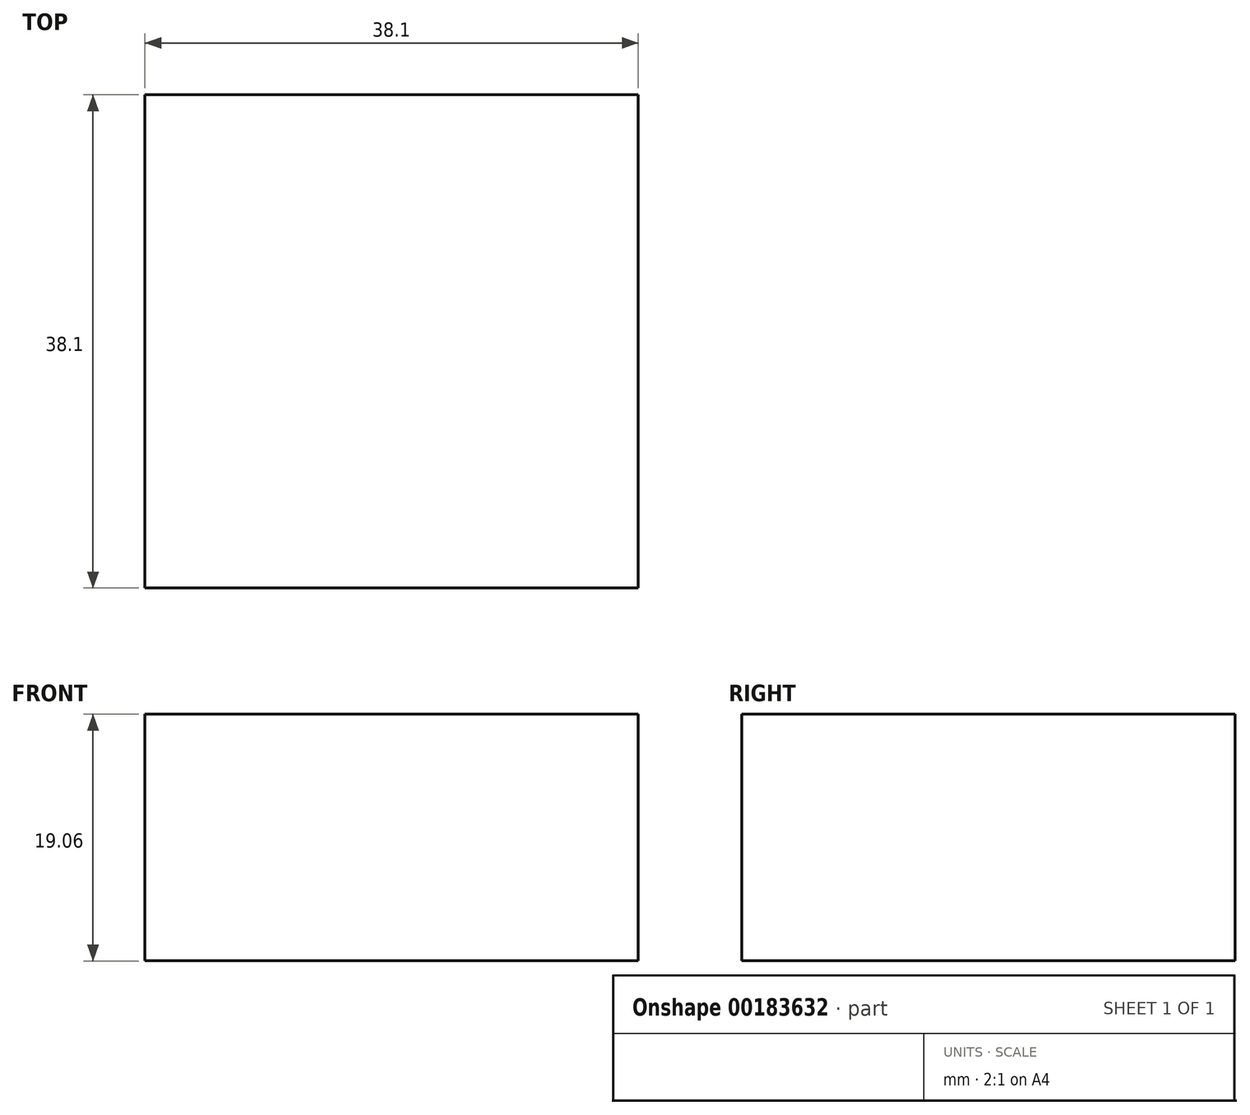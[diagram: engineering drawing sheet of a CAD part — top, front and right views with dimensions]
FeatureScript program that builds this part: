
annotation { "Feature Type Name" : "Feature", "Feature Type Description" : "" }
export const myFeature = defineFeature(function(context is Context, id is Id, definition is map)
    precondition{}
    {
        {
            var Q0;
            Q0=qCreatedBy(makeId("Front.planeOp"),FACE);
            var sketch = newSketch(context, id + "F0", { "sketchPlane" : qUnion([Q0])});
            skLineSegment(sketch, "E0.bottom", {"start": v(-19.05, 9.53) * mm, "end": v(19.05, 9.53) * mm});
            skLineSegment(sketch, "E0.top", {"start": v(-19.05, -9.53) * mm, "end": v(19.05, -9.53) * mm});
            skLineSegment(sketch, "E0.left", {"start": v(-19.05, 9.53) * mm, "end": v(-19.05, -9.53) * mm});
            skLineSegment(sketch, "E0.right", {"start": v(19.05, 9.53) * mm, "end": v(19.05, -9.53) * mm});
            skPoint(sketch, "E0.middle", {"position": v(0, 0) * mm});
            skSolve(sketch);
        }
        {
            var Q0;
            Q0=makeQuery(id+"F0.imprint","IMPRINT",FACE,{"disambiguationData":[TD([[makeQuery(id+"F0.imprint","IMPRINT",EDGE,{"derivedFrom":sQuery(id+"F0.wireOp",EDGE,"E0.bottom")}),-1.0]])]});
            extrude(context, id + "F1", {"entities" : qUnion([Q0]), "depth" : 19.05 * mm, "hasSecondDirection" : true, "secondDirectionOppositeDirection" : true, "secondDirectionDepth" : 19.05 * mm});
        }
    });
